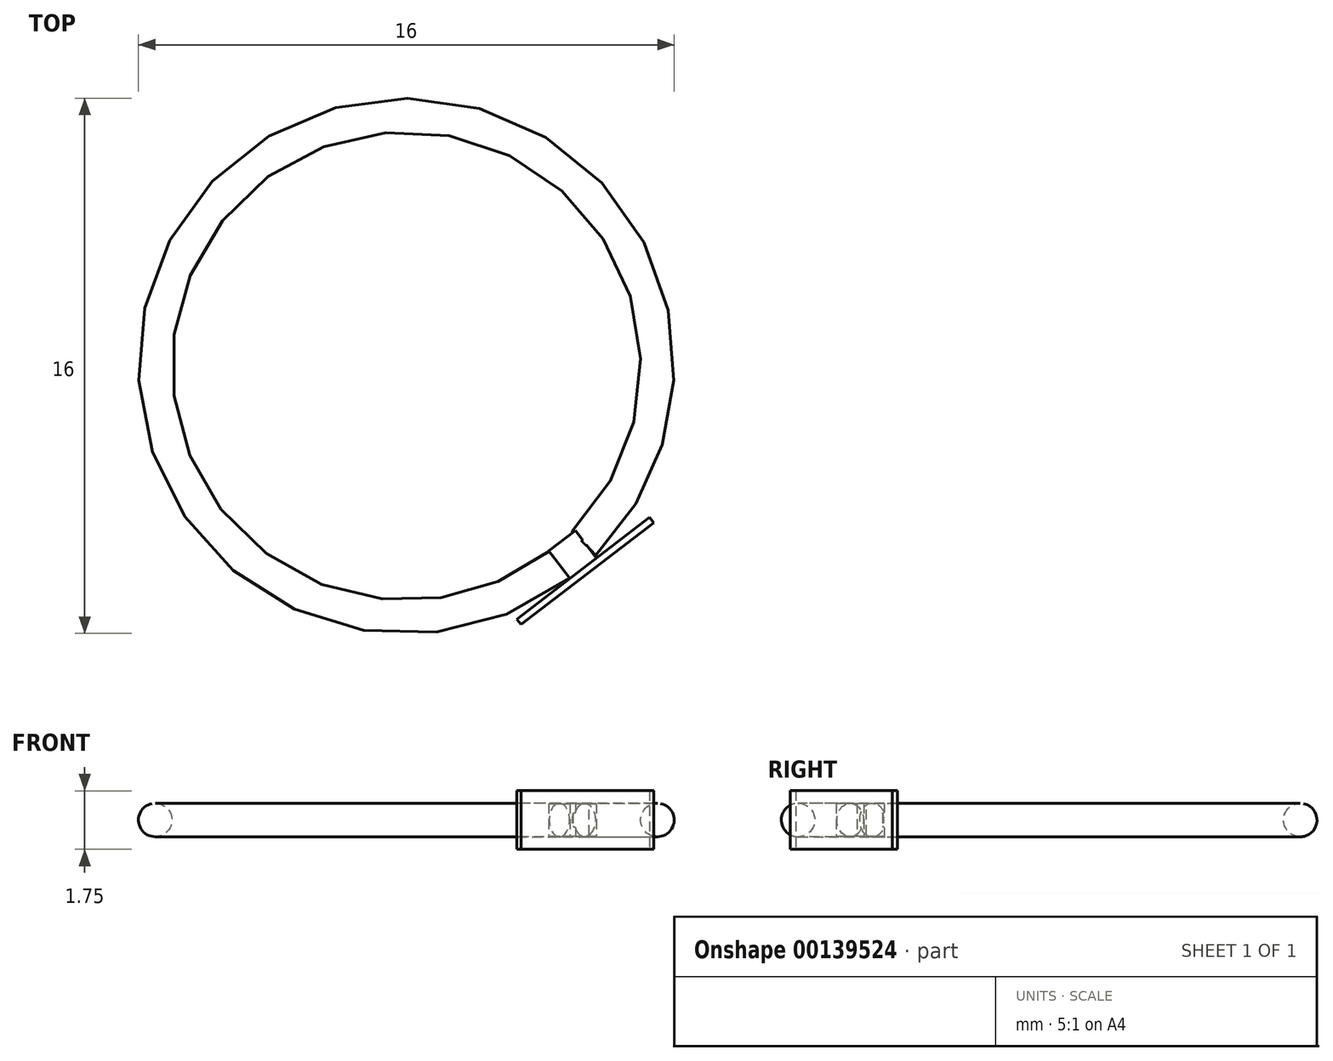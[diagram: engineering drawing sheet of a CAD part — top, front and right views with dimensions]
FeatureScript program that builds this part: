
annotation { "Feature Type Name" : "Feature", "Feature Type Description" : "" }
export const myFeature = defineFeature(function(context is Context, id is Id, definition is map)
    precondition{}
    {
        {
            var Q0;
            Q0=qCreatedBy(makeId("Front.planeOp"),FACE);
            var sketch = newSketch(context, id + "F0", { "sketchPlane" : qUnion([Q0])});
            skCircle(sketch, "E0", {"center": v(7.5, 24.29) * mm, "radius": 0.5 * mm});
            skSolve(sketch);
        }
        {
            var Q0;
            Q0=qCreatedBy(makeId("Front.planeOp"),FACE);
            var sketch = newSketch(context, id + "F1", { "sketchPlane" : qUnion([Q0])});
            skLineSegment(sketch, "E1", {"start": v(0, 42.87) * mm, "end": v(0, 13) * mm});
            skSolve(sketch);
        }
        {
            var Q0;
            Q0 = qSketchRegion(id + "F0", true);
            var Q1;
            Q1=sQuery(id+"F1.wireOp",EDGE,"E1");
            revolve(context, id + "F2", {"entities" : qUnion([Q0]), "axis" : qUnion([Q1]), "revolveType" : RevolveType.TWO_DIRECTIONS, "angle" : 45 * degree, "angleBack" : 52.44 * degree});
        }
        {
            var Q0;
            Q0=makeQuery(id+"F2.opRevolve","CAP_FACE",FACE,{"disambiguationData":[OSD([sQuery(id+"F0.wireOp",EDGE,"E0")])],"isStart":true});
            var sketch = newSketch(context, id + "F3", { "sketchPlane" : qUnion([Q0])});
            skLineSegment(sketch, "E2.bottom", {"start": v(-6.98, 24.78) * mm, "end": v(-8.02, 24.78) * mm});
            skLineSegment(sketch, "E2.top", {"start": v(-6.98, 23.8) * mm, "end": v(-8.02, 23.8) * mm});
            skLineSegment(sketch, "E2.left", {"start": v(-6.98, 24.78) * mm, "end": v(-6.98, 23.8) * mm});
            skLineSegment(sketch, "E2.right", {"start": v(-8.02, 24.78) * mm, "end": v(-8.02, 23.8) * mm});
            skPoint(sketch, "E2.middle", {"position": v(-7.5, 24.29) * mm});
            skSolve(sketch);
        }
        {
            var Q0;
            Q0 = qSketchRegion(id + "F3", true);
            extrude(context, id + "F4", {"entities" : qUnion([Q0]), "operationType" : NewBodyOperationType.ADD, "depth" : 1 * mm});
        }
        {
            var Q0;
            Q0=makeQuery(id+"F4.opExtrude","SWEPT_FACE",FACE,{"disambiguationData":[OSD([sQuery(id+"F3.wireOp",EDGE,"E2.right")])]});
            var sketch = newSketch(context, id + "F5", { "sketchPlane" : qUnion([Q0])});
            skLineSegment(sketch, "E3.bottom", {"start": v(3, 25.16) * mm, "end": v(-2, 25.16) * mm});
            skLineSegment(sketch, "E3.top", {"start": v(3, 23.41) * mm, "end": v(-2, 23.41) * mm});
            skLineSegment(sketch, "E3.left", {"start": v(3, 25.16) * mm, "end": v(3, 23.41) * mm});
            skLineSegment(sketch, "E3.right", {"start": v(-2, 25.16) * mm, "end": v(-2, 23.41) * mm});
            skPoint(sketch, "E3.middle", {"position": v(0.5, 24.29) * mm});
            skPoint(sketch, "E3.middle.positionSnap0", {"position": v(0.5, 23.8) * mm});
            skPoint(sketch, "E3.middle.positionSnap1", {"position": v(1, 24.29) * mm});
            skPoint(sketch, "E3.centerSnap0", {"position": v(0.5, 23.8) * mm});
            skPoint(sketch, "E3.centerSnap1", {"position": v(1, 24.29) * mm});
            skSolve(sketch);
        }
        {
            var Q0;
            Q0 = qSketchRegion(id + "F5", true);
            extrude(context, id + "F6", {"entities" : qUnion([Q0]), "operationType" : NewBodyOperationType.ADD, "depth" : 0.2 * mm});
        }
    });
